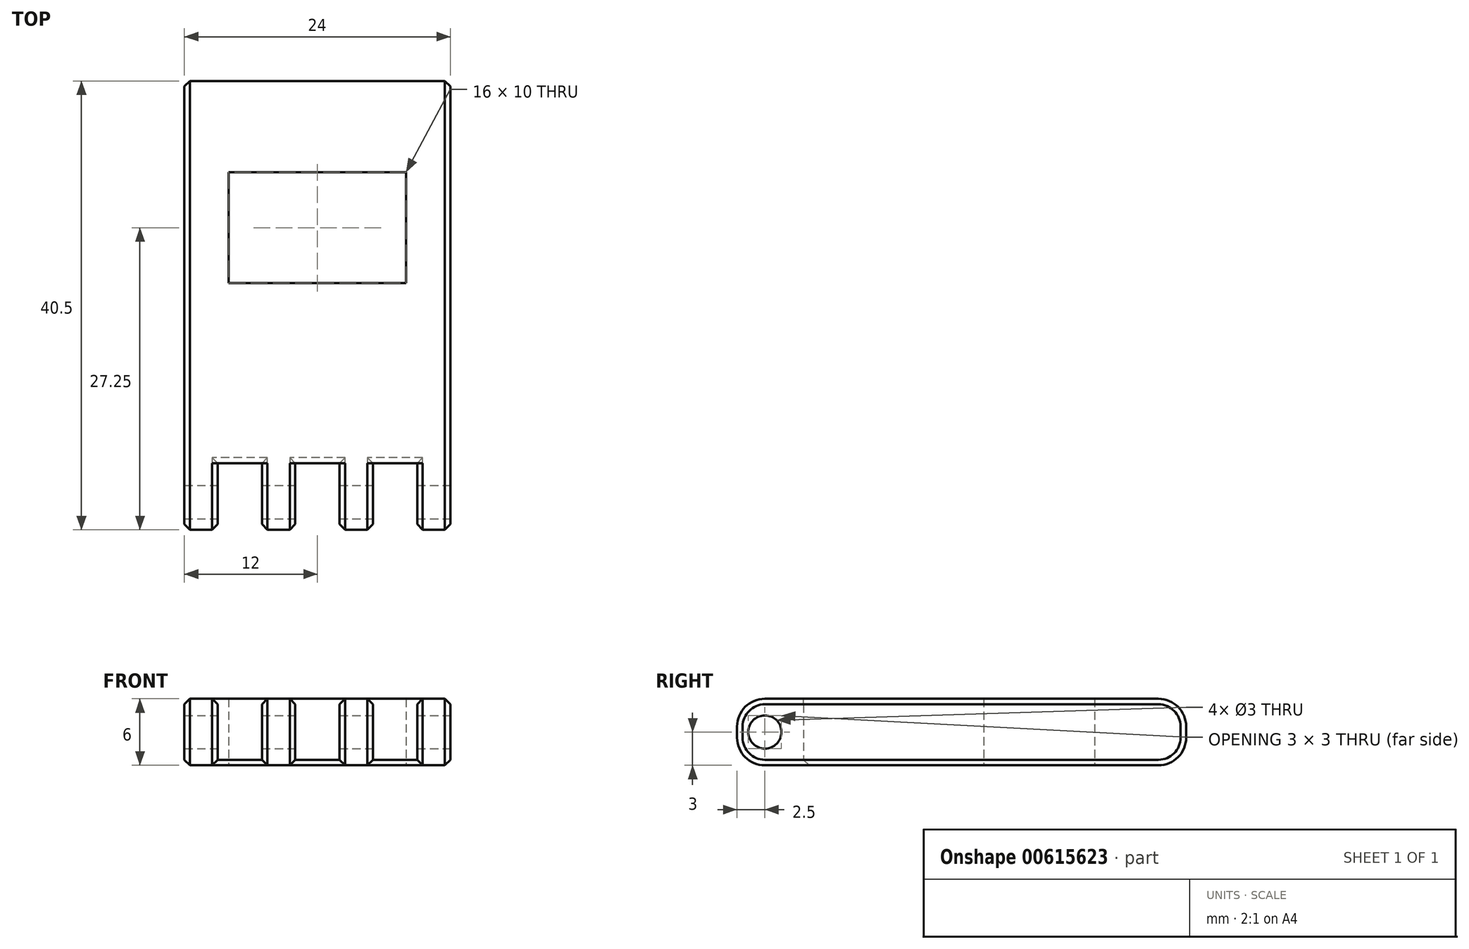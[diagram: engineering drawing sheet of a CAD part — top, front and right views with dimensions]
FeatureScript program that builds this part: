
annotation { "Feature Type Name" : "Feature", "Feature Type Description" : "" }
export const myFeature = defineFeature(function(context is Context, id is Id, definition is map)
    precondition{}
    {
        {
            var Q0;
            Q0=qCreatedBy(makeId("Top.planeOp"),FACE);
            var sketch = newSketch(context, id + "F0", { "sketchPlane" : qUnion([Q0])});
            skLineSegment(sketch, "E0.bottom", {"start": v(-12, 20.25) * mm, "end": v(12, 20.25) * mm});
            skLineSegment(sketch, "E0.top", {"start": v(-12, -20.25) * mm, "end": v(12, -20.25) * mm});
            skLineSegment(sketch, "E0.left", {"start": v(-12, 20.25) * mm, "end": v(-12, -20.25) * mm});
            skLineSegment(sketch, "E0.right", {"start": v(12, 20.25) * mm, "end": v(12, -20.25) * mm});
            skSolve(sketch);
        }
        {
            var Q0;
            Q0 = qSketchRegion(id + "F0", true);
            extrude(context, id + "F1", {"entities" : qUnion([Q0]), "endBound" : BoundingType.SYMMETRIC, "depth" : 6 * mm, "offsetDistance" : 25 * mm});
        }
        {
            var Q0;
            Q0=qCreatedBy(makeId("Right.planeOp"),FACE);
            var sketch = newSketch(context, id + "F2", { "sketchPlane" : qUnion([Q0])});
            skCircle(sketch, "E1", {"center": v(-17.75, 0) * mm, "radius": 1.5 * mm});
            skSolve(sketch);
        }
        {
            var Q0;
            Q0 = qSketchRegion(id + "F2", true);
            extrude(context, id + "F3", {"entities" : qUnion([Q0]), "operationType" : NewBodyOperationType.REMOVE, "endBound" : BoundingType.SYMMETRIC, "oppositeDirection" : true, "depth" : 50 * mm, "offsetDistance" : 25 * mm});
        }
        {
            var Q0;
            Q0=makeQuery(id+"F1.opExtrude","CAP_EDGE",EDGE,{"disambiguationData":[OSD([sQuery(id+"F0.wireOp",EDGE,"E0.top")])],"isStart":false});
            var Q1;
            Q1=makeQuery(id+"F1.opExtrude","CAP_EDGE",EDGE,{"disambiguationData":[OSD([sQuery(id+"F0.wireOp",EDGE,"E0.top")])],"isStart":true});
            var Q2;
            Q2=makeQuery(id+"F1.opExtrude","CAP_EDGE",EDGE,{"disambiguationData":[OSD([sQuery(id+"F0.wireOp",EDGE,"E0.bottom")])],"isStart":false});
            var Q3;
            Q3=makeQuery(id+"F1.opExtrude","CAP_EDGE",EDGE,{"disambiguationData":[OSD([sQuery(id+"F0.wireOp",EDGE,"E0.bottom")])],"isStart":true});
            fillet(context, id + "F4", {"entities" : qUnion([Q0, Q1, Q2, Q3]), "radius" : 2.5 * mm, "tangentPropagation" : true, "allowEdgeOverflow" : false});
        }
        {
            var Q0;
            Q0=qCreatedBy(makeId("Top.planeOp"),FACE);
            var sketch = newSketch(context, id + "F5", { "sketchPlane" : qUnion([Q0])});
            skLineSegment(sketch, "E2", {"start": v(2, -20.25) * mm, "end": v(-2, -20.25) * mm});
            skLineSegment(sketch, "E3", {"start": v(-9, -20.25) * mm, "end": v(-9, -14.25) * mm});
            skLineSegment(sketch, "E4", {"start": v(-9, -14.25) * mm, "end": v(-5, -14.25) * mm});
            skLineSegment(sketch, "E5", {"start": v(-5, -14.25) * mm, "end": v(-5, -20.25) * mm});
            skLineSegment(sketch, "E6", {"start": v(-2, -20.25) * mm, "end": v(-2, -14.25) * mm});
            skLineSegment(sketch, "E7", {"start": v(-2, -14.25) * mm, "end": v(2, -14.25) * mm});
            skLineSegment(sketch, "E8", {"start": v(2, -14.25) * mm, "end": v(2, -20.25) * mm});
            skLineSegment(sketch, "E9.trimOffspring", {"start": v(-5, -20.25) * mm, "end": v(-9, -20.25) * mm});
            skLineSegment(sketch, "E10.MirrorCS", {"start": v(9, -20.25) * mm, "end": v(9, -14.25) * mm});
            skLineSegment(sketch, "E11.MirrorCS", {"start": v(5, -20.25) * mm, "end": v(9, -20.25) * mm});
            skLineSegment(sketch, "E12.MirrorCS", {"start": v(9, -14.25) * mm, "end": v(5, -14.25) * mm});
            skLineSegment(sketch, "E13.MirrorCS", {"start": v(5, -14.25) * mm, "end": v(5, -20.25) * mm});
            skSolve(sketch);
        }
        {
            var Q0;
            Q0 = qSketchRegion(id + "F5", true);
            extrude(context, id + "F6", {"entities" : qUnion([Q0]), "operationType" : NewBodyOperationType.REMOVE, "endBound" : BoundingType.SYMMETRIC, "depth" : 25 * mm, "offsetDistance" : 25 * mm});
        }
        {
            var Q0;
            Q0=qCreatedBy(makeId("Top.planeOp"),FACE);
            var sketch = newSketch(context, id + "F7", { "sketchPlane" : qUnion([Q0])});
            skLineSegment(sketch, "E14.bottom", {"start": v(-8, 12) * mm, "end": v(8, 12) * mm});
            skLineSegment(sketch, "E14.top", {"start": v(-8, 2) * mm, "end": v(8, 2) * mm});
            skLineSegment(sketch, "E14.left", {"start": v(-8, 12) * mm, "end": v(-8, 2) * mm});
            skLineSegment(sketch, "E14.right", {"start": v(8, 12) * mm, "end": v(8, 2) * mm});
            skSolve(sketch);
        }
        {
            var Q0;
            Q0 = qSketchRegion(id + "F7", true);
            extrude(context, id + "F8", {"entities" : qUnion([Q0]), "operationType" : NewBodyOperationType.REMOVE, "endBound" : BoundingType.SYMMETRIC, "depth" : 25 * mm, "offsetDistance" : 25 * mm});
        }
        {
            var Q0;
            Q0=makeQuery(id+"F1.opExtrude","CAP_EDGE",EDGE,{"disambiguationData":[OSD([sQuery(id+"F0.wireOp",EDGE,"E0.right")])],"isStart":true});
            var Q1;
            {var subQ0=sQuery(id+"F0.wireOp",EDGE,"E0.top");Q1=makeQuery(id+"F6.boolean.opBoolean","INTERSECT",EDGE,{"derivedFrom":[makeQuery(id+"F4.opFillet","BLEND_FACE",FACE,{"disambiguationData":[OSD([subQ0]),TDD([makeQuery(id+"F1.opExtrude","CAP_EDGE",EDGE,{"disambiguationData":[OSD([subQ0])],"isStart":true})])]}),makeQuery(id+"F6.opExtrude","SWEPT_FACE",FACE,{"disambiguationData":[OSD([sQuery(id+"F5.wireOp",EDGE,"E10.MirrorCS")])]})]});}
            var Q2;
            {var subQ0=sQuery(id+"F0.wireOp",EDGE,"E0.top");Q2=makeQuery(id+"F6.boolean.opBoolean","INTERSECT",EDGE,{"derivedFrom":[makeQuery(id+"F4.opFillet","BLEND_FACE",FACE,{"disambiguationData":[OSD([subQ0]),TDD([makeQuery(id+"F1.opExtrude","CAP_EDGE",EDGE,{"disambiguationData":[OSD([subQ0])],"isStart":true})])]}),makeQuery(id+"F6.opExtrude","SWEPT_FACE",FACE,{"disambiguationData":[OSD([sQuery(id+"F5.wireOp",EDGE,"E13.MirrorCS")])]})]});}
            var Q3;
            {var subQ0=sQuery(id+"F0.wireOp",EDGE,"E0.top");Q3=makeQuery(id+"F6.boolean.opBoolean","INTERSECT",EDGE,{"derivedFrom":[makeQuery(id+"F4.opFillet","BLEND_FACE",FACE,{"disambiguationData":[OSD([subQ0]),TDD([makeQuery(id+"F1.opExtrude","CAP_EDGE",EDGE,{"disambiguationData":[OSD([subQ0])],"isStart":true})])]}),makeQuery(id+"F6.opExtrude","SWEPT_FACE",FACE,{"disambiguationData":[OSD([sQuery(id+"F5.wireOp",EDGE,"E8")])]})]});}
            var Q4;
            {var subQ0=sQuery(id+"F0.wireOp",EDGE,"E0.top");Q4=makeQuery(id+"F6.boolean.opBoolean","INTERSECT",EDGE,{"derivedFrom":[makeQuery(id+"F4.opFillet","BLEND_FACE",FACE,{"disambiguationData":[OSD([subQ0]),TDD([makeQuery(id+"F1.opExtrude","CAP_EDGE",EDGE,{"disambiguationData":[OSD([subQ0])],"isStart":true})])]}),makeQuery(id+"F6.opExtrude","SWEPT_FACE",FACE,{"disambiguationData":[OSD([sQuery(id+"F5.wireOp",EDGE,"E6")])]})]});}
            var Q5;
            Q5=makeQuery(id+"F6.boolean.opBoolean","INTERSECT",EDGE,{"derivedFrom":[makeQuery(id+"F1.opExtrude","CAP_FACE",FACE,{"disambiguationData":[OSD([sQuery(id+"F0.wireOp",EDGE,"E0.bottom"),sQuery(id+"F0.wireOp",EDGE,"E0.top"),sQuery(id+"F0.wireOp",EDGE,"E0.left"),sQuery(id+"F0.wireOp",EDGE,"E0.right")])],"isStart":true}),makeQuery(id+"F6.opExtrude","SWEPT_FACE",FACE,{"disambiguationData":[OSD([sQuery(id+"F5.wireOp",EDGE,"E4")])]})]});
            var Q6;
            {var subQ0=sQuery(id+"F0.wireOp",EDGE,"E0.top");Q6=makeQuery(id+"F6.boolean.opBoolean","INTERSECT",EDGE,{"derivedFrom":[makeQuery(id+"F4.opFillet","BLEND_FACE",FACE,{"disambiguationData":[OSD([subQ0]),TDD([makeQuery(id+"F1.opExtrude","CAP_EDGE",EDGE,{"disambiguationData":[OSD([subQ0])],"isStart":true})])]}),makeQuery(id+"F6.opExtrude","SWEPT_FACE",FACE,{"disambiguationData":[OSD([sQuery(id+"F5.wireOp",EDGE,"E5")])]})]});}
            var Q7;
            {var subQ0=sQuery(id+"F0.wireOp",EDGE,"E0.top");Q7=makeQuery(id+"F6.boolean.opBoolean","INTERSECT",EDGE,{"derivedFrom":[makeQuery(id+"F4.opFillet","BLEND_FACE",FACE,{"disambiguationData":[OSD([subQ0]),TDD([makeQuery(id+"F1.opExtrude","CAP_EDGE",EDGE,{"disambiguationData":[OSD([subQ0])],"isStart":true})])]}),makeQuery(id+"F6.opExtrude","SWEPT_FACE",FACE,{"disambiguationData":[OSD([sQuery(id+"F5.wireOp",EDGE,"E3")])]})]});}
            var Q8;
            Q8=makeQuery(id+"F4.opFillet","BLEND_EDGE",EDGE,{"blendedFrom":[makeQuery(id+"F1.opExtrude","CAP_EDGE",EDGE,{"disambiguationData":[OSD([sQuery(id+"F0.wireOp",EDGE,"E0.top")])],"isStart":true}),makeQuery(id+"F1.opExtrude","SWEPT_FACE",FACE,{"disambiguationData":[OSD([sQuery(id+"F0.wireOp",EDGE,"E0.left")])]})],"blendedInto":[makeQuery(id+"F1.opExtrude","SWEPT_FACE",FACE,{"disambiguationData":[OSD([sQuery(id+"F0.wireOp",EDGE,"E0.left")])]})]});
            var Q9;
            Q9=makeQuery(id+"F6.boolean.opBoolean","INTERSECT",EDGE,{"derivedFrom":[makeQuery(id+"F1.opExtrude","CAP_FACE",FACE,{"disambiguationData":[OSD([sQuery(id+"F0.wireOp",EDGE,"E0.bottom"),sQuery(id+"F0.wireOp",EDGE,"E0.top"),sQuery(id+"F0.wireOp",EDGE,"E0.left"),sQuery(id+"F0.wireOp",EDGE,"E0.right")])],"isStart":true}),makeQuery(id+"F6.opExtrude","SWEPT_FACE",FACE,{"disambiguationData":[OSD([sQuery(id+"F5.wireOp",EDGE,"E7")])]})]});
            var Q10;
            Q10=makeQuery(id+"F6.boolean.opBoolean","INTERSECT",EDGE,{"derivedFrom":[makeQuery(id+"F1.opExtrude","CAP_FACE",FACE,{"disambiguationData":[OSD([sQuery(id+"F0.wireOp",EDGE,"E0.bottom"),sQuery(id+"F0.wireOp",EDGE,"E0.top"),sQuery(id+"F0.wireOp",EDGE,"E0.left"),sQuery(id+"F0.wireOp",EDGE,"E0.right")])],"isStart":true}),makeQuery(id+"F6.opExtrude","SWEPT_FACE",FACE,{"disambiguationData":[OSD([sQuery(id+"F5.wireOp",EDGE,"E12.MirrorCS")])]})]});
            chamfer(context, id + "F9", {"entities" : qUnion([Q0, Q1, Q2, Q3, Q4, Q5, Q6, Q7, Q8, Q9, Q10]), "width" : .5 * mm, "tangentPropagation" : true});
        }
    });
